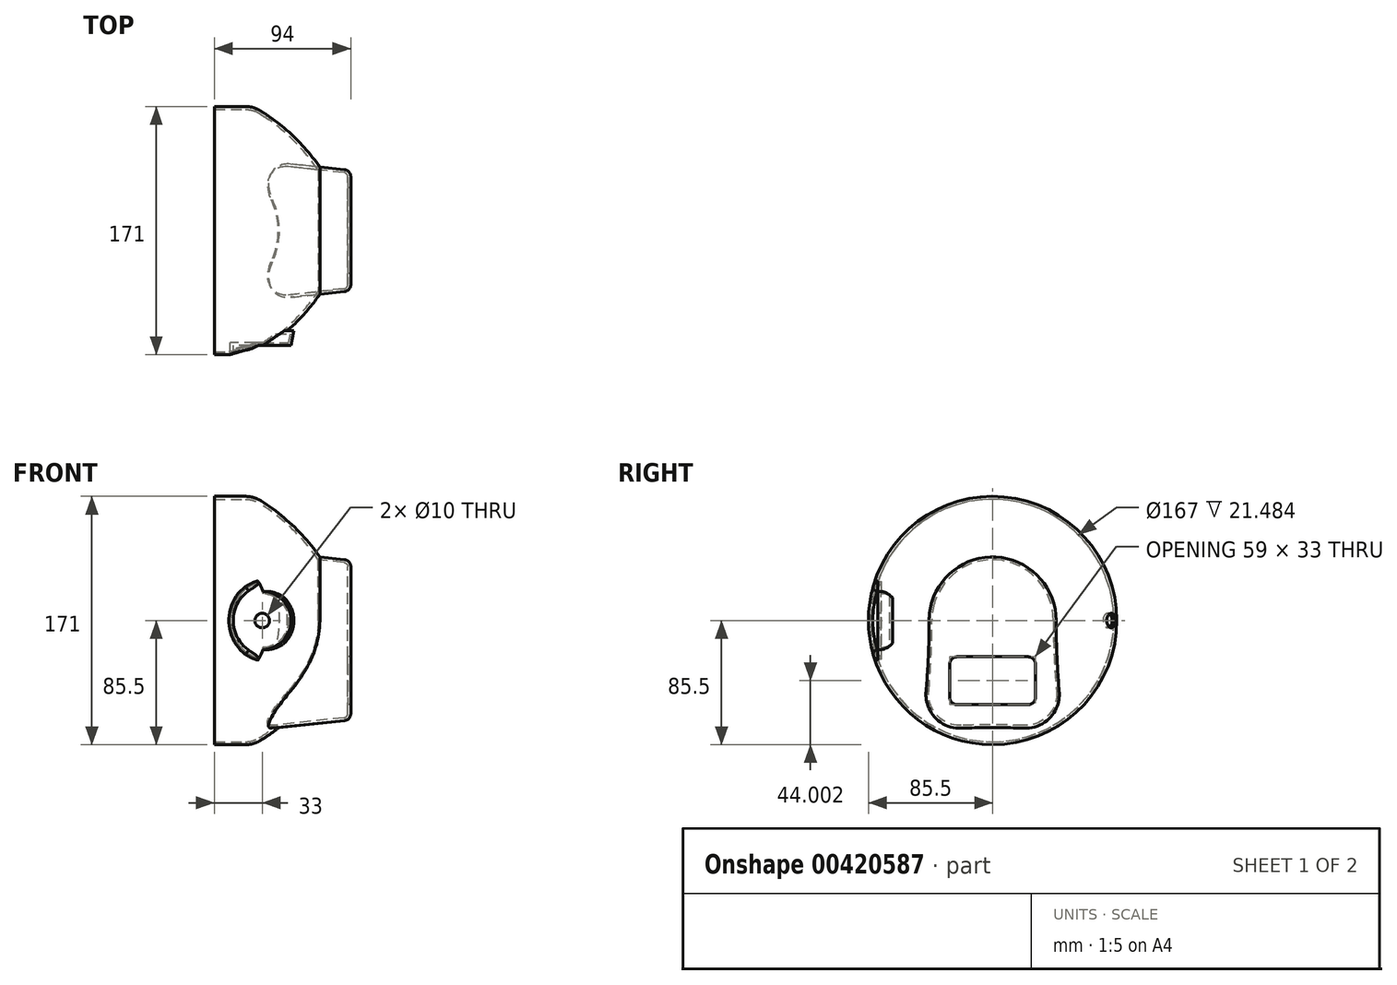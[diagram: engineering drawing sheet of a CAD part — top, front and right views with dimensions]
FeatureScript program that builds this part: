
annotation { "Feature Type Name" : "Feature", "Feature Type Description" : "" }
export const myFeature = defineFeature(function(context is Context, id is Id, definition is map)
    precondition{}
    {
        {
            var Q0;
            Q0=qCreatedBy(makeId("Front.planeOp"),FACE);
            var sketch = newSketch(context, id + "F0", { "sketchPlane" : qUnion([Q0])});
            skLineSegment(sketch, "E0", {"start": v(0, 0) * mm, "end": v(-132.16, 0) * mm, "construction": true});
            skLineSegment(sketch, "E1", {"start": v(-93, 0) * mm, "end": v(-93, 85.5) * mm});
            skLineSegment(sketch, "E2", {"start": v(-93, 85.5) * mm, "end": v(-66, 85.5) * mm});
            skLineSegment(sketch, "E3", {"start": v(-93, 0) * mm, "end": v(0, 0) * mm});
            skArc(sketch, "E4", {"start": v(0, 0) * mm, "mid": v(-24.43, 49.36) * mm, "end": v(-66, 85.5) * mm});
            skLineSegment(sketch, "E5", {"start": v(0, 0) * mm, "end": v(-20.64, 77.02) * mm, "construction": true});
            skSolve(sketch);
        }
        {
            var Q0;
            Q0 = qSketchRegion(id + "F0", true);
            var Q1;
            Q1=sQuery(id+"F0.wireOp",EDGE,"E0");
            revolve(context, id + "F1", {"surfaceOperationType" : NewSurfaceOperationType.NEW, "entities" : qUnion([Q0]), "axis" : qUnion([Q1]), "revolveType" : RevolveType.FULL});
        }
        {
            var Q0;
            Q0=qCreatedBy(makeId("Right.planeOp"),FACE);
            cPlane(context, id + "F2", {"entities" : qUnion([Q0]), "cplaneType" : CPlaneType.OFFSET, "offset" : 1 * mm, "width" : 150 * mm, "height" : 150 * mm});
        }
        {
            var Q0;
            Q0=qCreatedBy(id+"F2.planeOp",FACE);
            var sketch = newSketch(context, id + "F3", { "sketchPlane" : qUnion([Q0])});
            skArc(sketch, "E6", {"start": v(41.5, 0) * mm, "mid": v(0, 41.5) * mm, "end": v(-41.5, 0) * mm});
            skLineSegment(sketch, "E7.bottom", {"start": v(-41.5, 0) * mm, "end": v(41.5, 0) * mm, "construction": true});
            skLineSegment(sketch, "E7.top", {"start": v(-41.5, -68.5) * mm, "end": v(41.5, -68.5) * mm, "construction": true});
            skLineSegment(sketch, "E7.left", {"start": v(-41.5, 0) * mm, "end": v(-41.5, -68.5) * mm, "construction": true});
            skLineSegment(sketch, "E7.right", {"start": v(41.5, 0) * mm, "end": v(41.5, -68.5) * mm, "construction": true});
            skPoint(sketch, "E7.middle", {"position": v(0, -34.25) * mm});
            skLineSegment(sketch, "E8", {"start": v(-43.76, 41.5) * mm, "end": v(41.82, 41.5) * mm, "construction": true});
            skLineSegment(sketch, "E9", {"start": v(-41.5, 0) * mm, "end": v(-41.5, -48.5) * mm});
            skLineSegment(sketch, "E10", {"start": v(-21.5, -68.5) * mm, "end": v(21.5, -68.5) * mm});
            skLineSegment(sketch, "E11", {"start": v(41.5, -48.5) * mm, "end": v(41.5, 0) * mm});
            skArc(sketch, "E12", {"start": v(-41.5, -48.5) * mm, "mid": v(-35.64, -62.64) * mm, "end": v(-21.5, -68.5) * mm});
            skArc(sketch, "E13", {"start": v(21.5, -68.5) * mm, "mid": v(35.64, -62.64) * mm, "end": v(41.5, -48.5) * mm});
            skSolve(sketch);
        }
        {
            var Q0;
            Q0 = qSketchRegion(id + "F3", true);
            extrude(context, id + "F4", {"entities" : qUnion([Q0]), "operationType" : NewBodyOperationType.ADD, "endBound" : BoundingType.UP_TO_NEXT, "oppositeDirection" : true, "depth" : 25 * mm, "offsetDistance" : 25 * mm, "hasDraft" : true, "draftAngle" : 6 * degree});
        }
        {
            var Q0;
            Q0=makeQuery(id+"F4.opExtrude","CAP_EDGE",EDGE,{"disambiguationData":[OSD([sQuery(id+"F3.wireOp",EDGE,"E12")])],"isStart":true});
            fillet(context, id + "F5", {"entities" : qUnion([Q0]), "tangentPropagation" : true, "radius" : 5 * mm, "defaultsChanged" : true, "vertexSettings" : [], "allowEdgeOverflow" : false});
        }
        {
            var Q0;
            Q0=makeQuery(id+"F1.opRevolve","SWEPT_EDGE",EDGE,{"disambiguationData":[OSD([sQuery(id+"F0.wireOp",EDGE,"E2"),sQuery(id+"F0.wireOp",EDGE,"E4")])]});
            fillet(context, id + "F6", {"entities" : qUnion([Q0]), "tangentPropagation" : true, "radius" : 20 * mm, "defaultsChanged" : true, "vertexSettings" : [], "allowEdgeOverflow" : false});
        }
        {
            var Q0;
            Q0=qCreatedBy(makeId("Front.planeOp"),FACE);
            cPlane(context, id + "F7", {"entities" : qUnion([Q0]), "cplaneType" : CPlaneType.OFFSET, "offset" : (158 / 2) * mm, "width" : 150 * mm, "height" : 150 * mm});
        }
        {
            var Q0;
            Q0=qCreatedBy(id+"F7.planeOp",FACE);
            var sketch = newSketch(context, id + "F8", { "sketchPlane" : qUnion([Q0])});
            skCircle(sketch, "E14", {"center": v(-60, 0) * mm, "radius": 20 * mm});
            skSolve(sketch);
        }
        {
            var Q0;
            Q0 = qSketchRegion(id + "F8", true);
            extrude(context, id + "F9", {"entities" : qUnion([Q0]), "operationType" : NewBodyOperationType.ADD, "oppositeDirection" : true, "depth" : 10 * mm, "offsetDistance" : 25 * mm, "hasDraft" : true, "draftAngle" : 10 * degree});
        }
        {
            var Q0;
            Q0=makeQuery(id+"F9.opExtrude","CAP_FACE",FACE,{"disambiguationData":[OSD([sQuery(id+"F8.wireOp",EDGE,"E14")])],"isStart":true});
            var sketch = newSketch(context, id + "F10", { "sketchPlane" : qUnion([Q0])});
            skCircle(sketch, "E15", {"center": v(-55, 0) * mm, "radius": 25 * mm});
            skSolve(sketch);
        }
        {
            var Q0;
            Q0 = qSketchRegion(id + "F10", true);
            extrude(context, id + "F11", {"entities" : qUnion([Q0]), "operationType" : NewBodyOperationType.REMOVE, "depth" : 25 * mm, "offsetDistance" : 25 * mm});
        }
        {
            var Q0;
            Q0=makeQuery(id+"FRfGsTBGx14MwqE_1.1.F11.boolean.opBoolean","INTERSECT",EDGE,{"derivedFrom":[makeQuery(id+"F1.opRevolve","SWEPT_FACE",FACE,{"disambiguationData":[OSD([sQuery(id+"F0.wireOp",EDGE,"E2")])]}),makeQuery(id+"FRfGsTBGx14MwqE_1.1.F11.opExtrude","SWEPT_FACE",FACE,{"disambiguationData":[OSD([sQuery(id+"F10.wireOp",EDGE,"E15")])]})]});
            var Q1;
            Q1=makeQuery(id+"F11.boolean.opBoolean","INTERSECT",EDGE,{"derivedFrom":[makeQuery(id+"F1.opRevolve","SWEPT_FACE",FACE,{"disambiguationData":[OSD([sQuery(id+"F0.wireOp",EDGE,"E2")])]}),makeQuery(id+"F11.opExtrude","SWEPT_FACE",FACE,{"disambiguationData":[OSD([sQuery(id+"F10.wireOp",EDGE,"E15")])]})]});
            fillet(context, id + "F12", {"entities" : qUnion([Q0, Q1]), "tangentPropagation" : true, "radius" : 3 * mm, "defaultsChanged" : true, "vertexSettings" : [], "allowEdgeOverflow" : false});
        }
        {
            var Q0;
            Q0=makeQuery(id+"F1.opRevolve","SWEPT_FACE",FACE,{"disambiguationData":[OSD([sQuery(id+"F0.wireOp",EDGE,"E1")])]});
            shell(context, id + "F13", {"entities" : qUnion([Q0]), "thickness" : 2 * mm});
        }
        {
            var Q0;
            Q0=makeQuery(id+"F13.opShell","OFFSET_FACE",FACE,{"disambiguationData":[OSD([sQuery(id+"F3.wireOp",EDGE,"E6"),sQuery(id+"F3.wireOp",EDGE,"E9"),sQuery(id+"F3.wireOp",EDGE,"E10"),sQuery(id+"F3.wireOp",EDGE,"E11"),sQuery(id+"F3.wireOp",EDGE,"E12"),sQuery(id+"F3.wireOp",EDGE,"E13")])]});
            var sketch = newSketch(context, id + "F14", { "sketchPlane" : qUnion([Q0])});
            skLineSegment(sketch, "E16.bottom", {"start": v(-29.5, -25) * mm, "end": v(29.5, -25) * mm});
            skLineSegment(sketch, "E16.top", {"start": v(-29.5, -58) * mm, "end": v(29.5, -58) * mm});
            skLineSegment(sketch, "E16.left", {"start": v(-29.5, -25) * mm, "end": v(-29.5, -58) * mm});
            skLineSegment(sketch, "E16.right", {"start": v(29.5, -25) * mm, "end": v(29.5, -58) * mm});
            skPoint(sketch, "E16.middle", {"position": v(0, -41.5) * mm});
            skSolve(sketch);
        }
        {
            var Q0;
            Q0 = qSketchRegion(id + "F14", true);
            extrude(context, id + "F15", {"entities" : qUnion([Q0]), "operationType" : NewBodyOperationType.REMOVE, "endBound" : BoundingType.THROUGH_ALL, "oppositeDirection" : true, "depth" : 25 * mm, "offsetDistance" : 25 * mm});
        }
        {
            var Q0;
            Q0=makeQuery(id+"F15.boolean.opBoolean","COPY",EDGE,{"derivedFrom":makeQuery(id+"F15.opExtrude","SWEPT_EDGE",EDGE,{"disambiguationData":[OSD([sQuery(id+"F14.wireOp",EDGE,"E16.top"),sQuery(id+"F14.wireOp",EDGE,"E16.right")])]})});
            var Q1;
            Q1=makeQuery(id+"F15.boolean.opBoolean","COPY",EDGE,{"derivedFrom":makeQuery(id+"F15.opExtrude","SWEPT_EDGE",EDGE,{"disambiguationData":[OSD([sQuery(id+"F14.wireOp",EDGE,"E16.bottom"),sQuery(id+"F14.wireOp",EDGE,"E16.right")])]})});
            var Q2;
            Q2=makeQuery(id+"F15.boolean.opBoolean","COPY",EDGE,{"derivedFrom":makeQuery(id+"F15.opExtrude","SWEPT_EDGE",EDGE,{"disambiguationData":[OSD([sQuery(id+"F14.wireOp",EDGE,"E16.bottom"),sQuery(id+"F14.wireOp",EDGE,"E16.left")])]})});
            var Q3;
            Q3=makeQuery(id+"F15.boolean.opBoolean","COPY",EDGE,{"derivedFrom":makeQuery(id+"F15.opExtrude","SWEPT_EDGE",EDGE,{"disambiguationData":[OSD([sQuery(id+"F14.wireOp",EDGE,"E16.top"),sQuery(id+"F14.wireOp",EDGE,"E16.left")])]})});
            fillet(context, id + "F16", {"entities" : qUnion([Q0, Q1, Q2, Q3]), "tangentPropagation" : true, "radius" : 5 * mm, "defaultsChanged" : false, "vertexSettings" : [], "allowEdgeOverflow" : false});
        }
        {
            var Q0;
            Q0=makeQuery(id+"F11.boolean.opBoolean","MERGE",FACE,{"derivedFrom":[makeQuery(id+"F9.opExtrude","CAP_FACE",FACE,{"disambiguationData":[OSD([sQuery(id+"F8.wireOp",EDGE,"E14")])],"isStart":true})],"fromTools":[makeQuery(id+"F11.opExtrude","CAP_FACE",FACE,{"disambiguationData":[OSD([sQuery(id+"F10.wireOp",EDGE,"E15")])],"isStart":true})]});
            var sketch = newSketch(context, id + "F17", { "sketchPlane" : qUnion([Q0])});
            skCircle(sketch, "E17", {"center": v(-60, 0) * mm, "radius": 5 * mm});
            skSolve(sketch);
        }
        {
            var Q0;
            Q0 = qSketchRegion(id + "F17", true);
            extrude(context, id + "F18", {"entities" : qUnion([Q0]), "operationType" : NewBodyOperationType.REMOVE, "endBound" : BoundingType.THROUGH_ALL, "oppositeDirection" : true, "depth" : 25 * mm, "offsetDistance" : 25 * mm});
        }
    });
